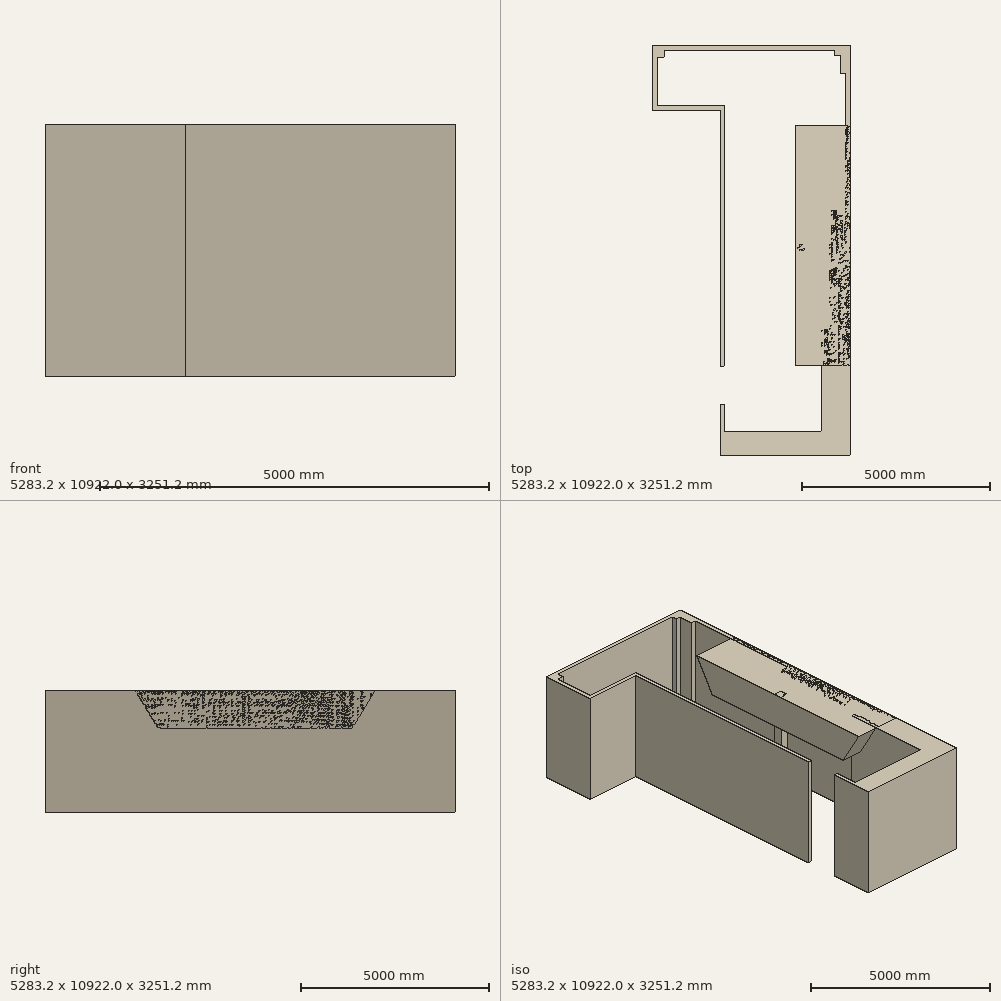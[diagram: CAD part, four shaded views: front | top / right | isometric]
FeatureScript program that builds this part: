
annotation { "Feature Type Name" : "Feature", "Feature Type Description" : "" }
export const myFeature = defineFeature(function(context is Context, id is Id, definition is map)
    precondition{}
    {
        {
            var Q0;
            Q0=qCreatedBy(makeId("Top.planeOp"),FACE);
            var sketch = newSketch(context, id + "F0", { "sketchPlane" : qUnion([Q0])});
            skLineSegment(sketch, "E0", {"start": v(-1612.9, 0) * mm, "end": v(1612.9, 0) * mm});
            skLineSegment(sketch, "E1", {"start": v(1612.9, 0) * mm, "end": v(1612.9, 10668) * mm});
            skLineSegment(sketch, "E2", {"start": v(1612.9, 10668) * mm, "end": v(-3416.3, 10668) * mm});
            skLineSegment(sketch, "E3", {"start": v(-3416.3, 10668) * mm, "end": v(-3416.3, 9194.8) * mm});
            skLineSegment(sketch, "E4", {"start": v(-3416.3, 9194.8) * mm, "end": v(-1612.9, 9194.8) * mm});
            skLineSegment(sketch, "E5", {"start": v(-1612.9, 9194.8) * mm, "end": v(-1612.9, 2235.2) * mm});
            skPoint(sketch, "E6", {"position": v(-1612.9, 1219.2) * mm});
            skPoint(sketch, "E7", {"position": v(-1612.9, 2235.2) * mm});
            skLineSegment(sketch, "E8", {"start": v(952.5, 0) * mm, "end": v(952.5, 3225.8) * mm});
            skLineSegment(sketch, "E9", {"start": v(952.5, 3225.8) * mm, "end": v(1181.1, 3225.8) * mm});
            skLineSegment(sketch, "E10.bottom", {"start": v(266.7, 5588) * mm, "end": v(520.7, 5588) * mm});
            skLineSegment(sketch, "E10.top", {"start": v(266.7, 5334) * mm, "end": v(520.7, 5334) * mm});
            skLineSegment(sketch, "E10.left", {"start": v(266.7, 5588) * mm, "end": v(266.7, 5334) * mm});
            skLineSegment(sketch, "E10.right", {"start": v(520.7, 5588) * mm, "end": v(520.7, 5334) * mm});
            skPoint(sketch, "E11", {"position": v(0, 0) * mm});
            skLineSegment(sketch, "E12.trimOffspring", {"start": v(-1612.9, 1219.2) * mm, "end": v(-1612.9, 0) * mm});
            skLineSegment(sketch, "E13", {"start": v(-3416.3, 10464.8) * mm, "end": v(-3213.1, 10464.8) * mm});
            skLineSegment(sketch, "E14", {"start": v(-3213.1, 10464.8) * mm, "end": v(-3213.1, 10668) * mm});
            skLineSegment(sketch, "E15", {"start": v(1460.5, 10515.6) * mm, "end": v(1460.5, 10058.4) * mm});
            skLineSegment(sketch, "E16", {"start": v(1460.5, 10058.4) * mm, "end": v(1612.9, 10058.4) * mm});
            skLineSegment(sketch, "E17", {"start": v(1460.5, 10515.6) * mm, "end": v(1308.1, 10515.6) * mm});
            skLineSegment(sketch, "E18", {"start": v(1308.1, 10515.6) * mm, "end": v(1308.1, 10668) * mm});
            skLineSegment(sketch, "E19", {"start": v(1181.1, 3225.8) * mm, "end": v(1181.1, 6400.8) * mm});
            skLineSegment(sketch, "E20", {"start": v(1181.1, 6400.8) * mm, "end": v(1612.9, 6400.8) * mm});
            skLineSegment(sketch, "E21.0", {"start": v(-1739.9, 9067.8) * mm, "end": v(-1739.9, 2235.2) * mm});
            skLineSegment(sketch, "E21.1", {"start": v(-3543.3, 9067.8) * mm, "end": v(-1739.9, 9067.8) * mm});
            skLineSegment(sketch, "E21.2", {"start": v(-3543.3, 10795) * mm, "end": v(-3543.3, 9067.8) * mm});
            skLineSegment(sketch, "E21.3", {"start": v(-1739.9, 1219.2) * mm, "end": v(-1739.9, -127) * mm});
            skLineSegment(sketch, "E21.4", {"start": v(-1739.9, -127) * mm, "end": v(1739.9, -127) * mm});
            skLineSegment(sketch, "E21.5", {"start": v(1739.9, -127) * mm, "end": v(1739.9, 10795) * mm});
            skLineSegment(sketch, "E21.6", {"start": v(1739.9, 10795) * mm, "end": v(-3543.3, 10795) * mm});
            skLineSegment(sketch, "E22", {"start": v(-1739.9, 1219.2) * mm, "end": v(-1612.9, 1219.2) * mm});
            skLineSegment(sketch, "E23", {"start": v(-1739.9, 2235.2) * mm, "end": v(-1612.9, 2235.2) * mm});
            skSolve(sketch);
        }
        {
            var Q0;
            Q0 = qSketchRegion(id + "F0", true);
            extrude(context, id + "F1", {"entities" : qUnion([Q0]), "depth" : 3251.2 * mm, "offsetDistance" : 25.4 * mm});
        }
        {
            var Q0;
            Q0=makeQuery(id+"F1.opExtrude","SWEPT_FACE",FACE,{"disambiguationData":[OSD([sQuery(id+"F0.wireOp",EDGE,"E0")])]});
            var sketch = newSketch(context, id + "F2", { "sketchPlane" : qUnion([Q0])});
            skLineSegment(sketch, "E24.bottom", {"start": v(-1739.9, 3251.2) * mm, "end": v(1739.9, 3251.2) * mm});
            skLineSegment(sketch, "E24.top", {"start": v(-1739.9, 3022.6) * mm, "end": v(1739.9, 3022.6) * mm});
            skLineSegment(sketch, "E24.left", {"start": v(1739.9, 3251.2) * mm, "end": v(1739.9, 3022.6) * mm});
            skLineSegment(sketch, "E24.right", {"start": v(-1739.9, 3251.2) * mm, "end": v(-1739.9, 3022.6) * mm});
            skSolve(sketch);
        }
        {
            var Q0;
            Q0 = qSketchRegion(id + "F2", true);
            extrude(context, id + "F3", {"entities" : qUnion([Q0]), "operationType" : NewBodyOperationType.ADD, "depth" : 508 * mm, "offsetDistance" : 25.4 * mm});
        }
        {
            var Q0;
            Q0=makeQuery(id+"F1.opExtrude","CAP_FACE",FACE,{"disambiguationData":[OSD([sQuery(id+"F0.wireOp",EDGE,"E10.bottom"),sQuery(id+"F0.wireOp",EDGE,"E10.top"),sQuery(id+"F0.wireOp",EDGE,"E10.left"),sQuery(id+"F0.wireOp",EDGE,"E10.right")])],"isStart":false});
            var sketch = newSketch(context, id + "F4", { "sketchPlane" : qUnion([Q0])});
            skLineSegment(sketch, "E25", {"start": v(266.7, 5461) * mm, "end": v(1739.9, 5461) * mm, "construction": true});
            skSolve(sketch);
        }
        {
            var Q0;
            Q0=makeQuery(id+"F1.opExtrude","SWEPT_FACE",FACE,{"disambiguationData":[OSD([sQuery(id+"F0.wireOp",EDGE,"E21.5")])]});
            var sketch = newSketch(context, id + "F5", { "sketchPlane" : qUnion([Q0])});
            skLineSegment(sketch, "E26", {"start": v(10795, 3251.2) * mm, "end": v(8661.4, 3251.2) * mm, "construction": true});
            skLineSegment(sketch, "E27", {"start": v(8661.4, 3251.2) * mm, "end": v(8051.8, 2235.2) * mm});
            skLineSegment(sketch, "E28", {"start": v(8051.8, 2235.2) * mm, "end": v(2870.2, 2235.2) * mm});
            skLineSegment(sketch, "E29", {"start": v(2870.2, 2235.2) * mm, "end": v(2260.6, 3251.2) * mm});
            skLineSegment(sketch, "E30", {"start": v(2260.6, 3251.2) * mm, "end": v(8661.4, 3251.2) * mm});
            skLineSegment(sketch, "E31", {"start": v(5461, 2235.2) * mm, "end": v(5461, 3251.2) * mm, "construction": true});
            skSolve(sketch);
        }
        {
            var Q0;
            Q0 = qSketchRegion(id + "F5", true);
            var Q1;
            Q1=makeQuery(id+"F1.opExtrude","SWEPT_FACE",FACE,{"disambiguationData":[OSD([sQuery(id+"F0.wireOp",EDGE,"E10.left")])]});
            extrude(context, id + "F6", {"entities" : qUnion([Q0]), "endBound" : BoundingType.UP_TO_SURFACE, "oppositeDirection" : true, "depth" : 406.4 * mm, "endBoundEntityFace" : qUnion([Q1]), "offsetDistance" : 25.4 * mm});
        }
    });
